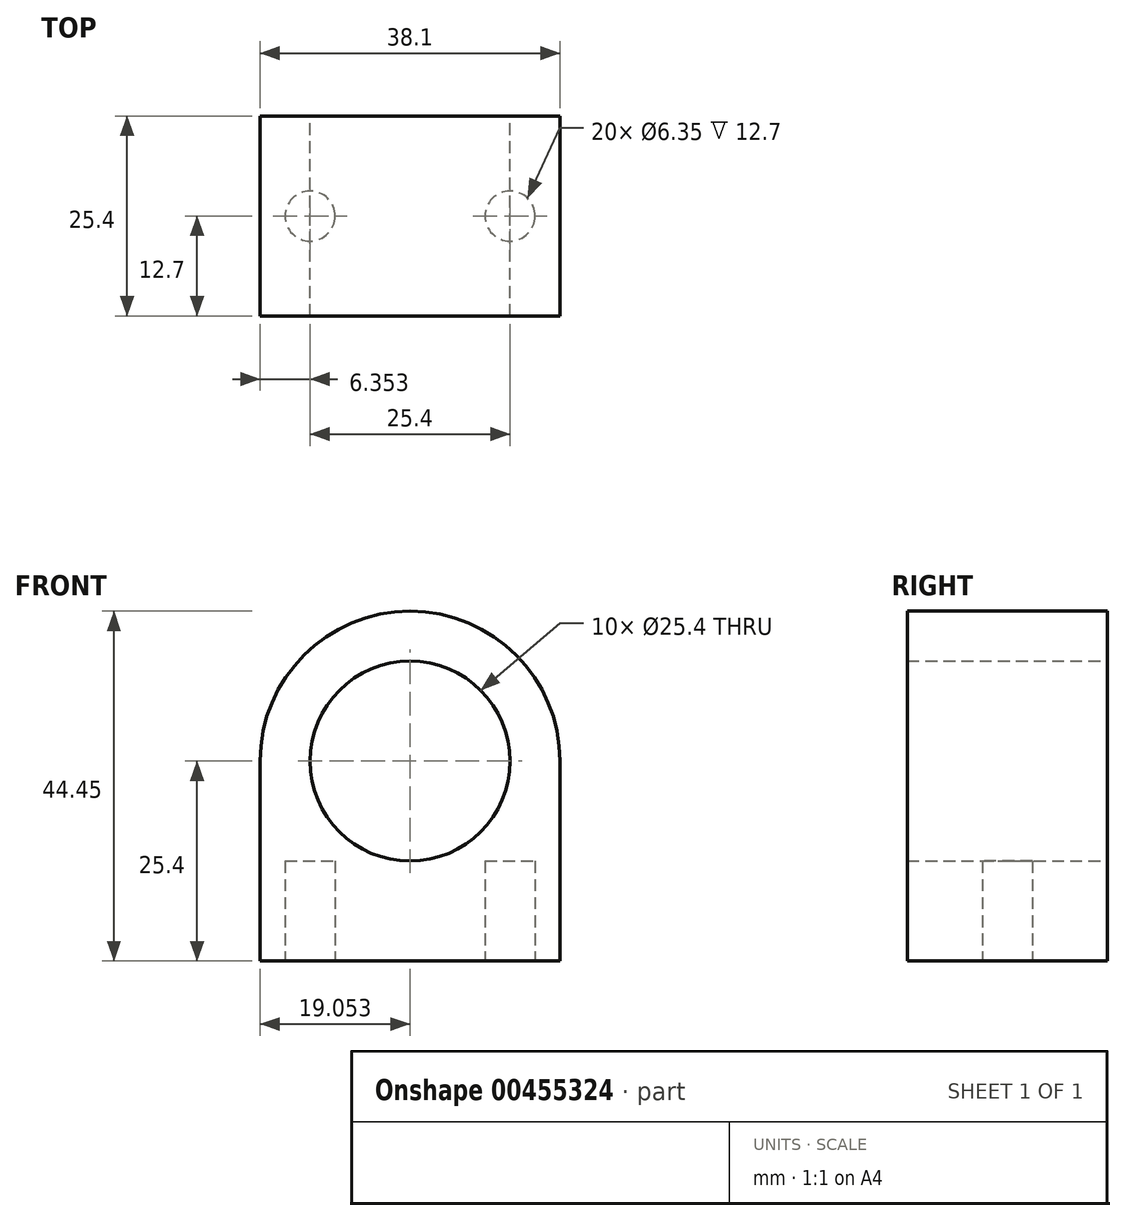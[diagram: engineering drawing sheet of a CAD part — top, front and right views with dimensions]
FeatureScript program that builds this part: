
annotation { "Feature Type Name" : "Feature", "Feature Type Description" : "" }
export const myFeature = defineFeature(function(context is Context, id is Id, definition is map)
    precondition{}
    {
        {
            var Q0;
            Q0=qCreatedBy(makeId("Front.planeOp"),FACE);
            var sketch = newSketch(context, id + "F0", { "sketchPlane" : qUnion([Q0])});
            skLineSegment(sketch, "E0.top", {"start": v(-12.64, -12.7) * mm, "end": v(25.46, -12.7) * mm});
            skLineSegment(sketch, "E0.left", {"start": v(-12.64, 12.7) * mm, "end": v(-12.64, -12.7) * mm});
            skLineSegment(sketch, "E0.right", {"start": v(25.46, 12.7) * mm, "end": v(25.46, -12.7) * mm});
            skArc(sketch, "E1", {"start": v(25.46, 12.7) * mm, "mid": v(6.41, 31.75) * mm, "end": v(-12.64, 12.7) * mm});
            skCircle(sketch, "E2", {"center": v(6.41, 12.7) * mm, "radius": 12.7 * mm});
            skSolve(sketch);
        }
        {
            var Q0;
            Q0=makeQuery(id+"F0.imprint","IMPRINT",FACE,{"disambiguationData":[TD([[makeQuery(id+"F0.imprint","IMPRINT",EDGE,{"derivedFrom":sQuery(id+"F0.wireOp",EDGE,"E0.top")}),1.0]])]});
            extrude(context, id + "F1", {"entities" : qUnion([Q0]), "depth" : 25.4 * mm});
        }
        {
            var Q0;
            Q0=makeQuery(id+"F1.opExtrude","SWEPT_FACE",FACE,{"disambiguationData":[OSD([sQuery(id+"F0.wireOp",EDGE,"E0.top")])]});
            var sketch = newSketch(context, id + "F2", { "sketchPlane" : qUnion([Q0])});
            skCircle(sketch, "E3", {"center": v(-6.29, 12.7) * mm, "radius": 3.18 * mm});
            skCircle(sketch, "E4", {"center": v(19.11, 12.7) * mm, "radius": 3.18 * mm});
            skSolve(sketch);
        }
        {
            var Q0;
            Q0=makeQuery(id+"F2.imprint","IMPRINT",FACE,{"disambiguationData":[TD([[makeQuery(id+"F2.imprint","IMPRINT",EDGE,{"derivedFrom":sQuery(id+"F2.wireOp",EDGE,"E3")}),1.0]])]});
            var Q1;
            Q1=makeQuery(id+"F2.imprint","IMPRINT",FACE,{"disambiguationData":[TD([[makeQuery(id+"F2.imprint","IMPRINT",EDGE,{"derivedFrom":sQuery(id+"F2.wireOp",EDGE,"E4")}),1.0]])]});
            extrude(context, id + "F3", {"entities" : qUnion([Q0, Q1]), "operationType" : NewBodyOperationType.REMOVE, "oppositeDirection" : true, "depth" : 12.7 * mm});
        }
    });
